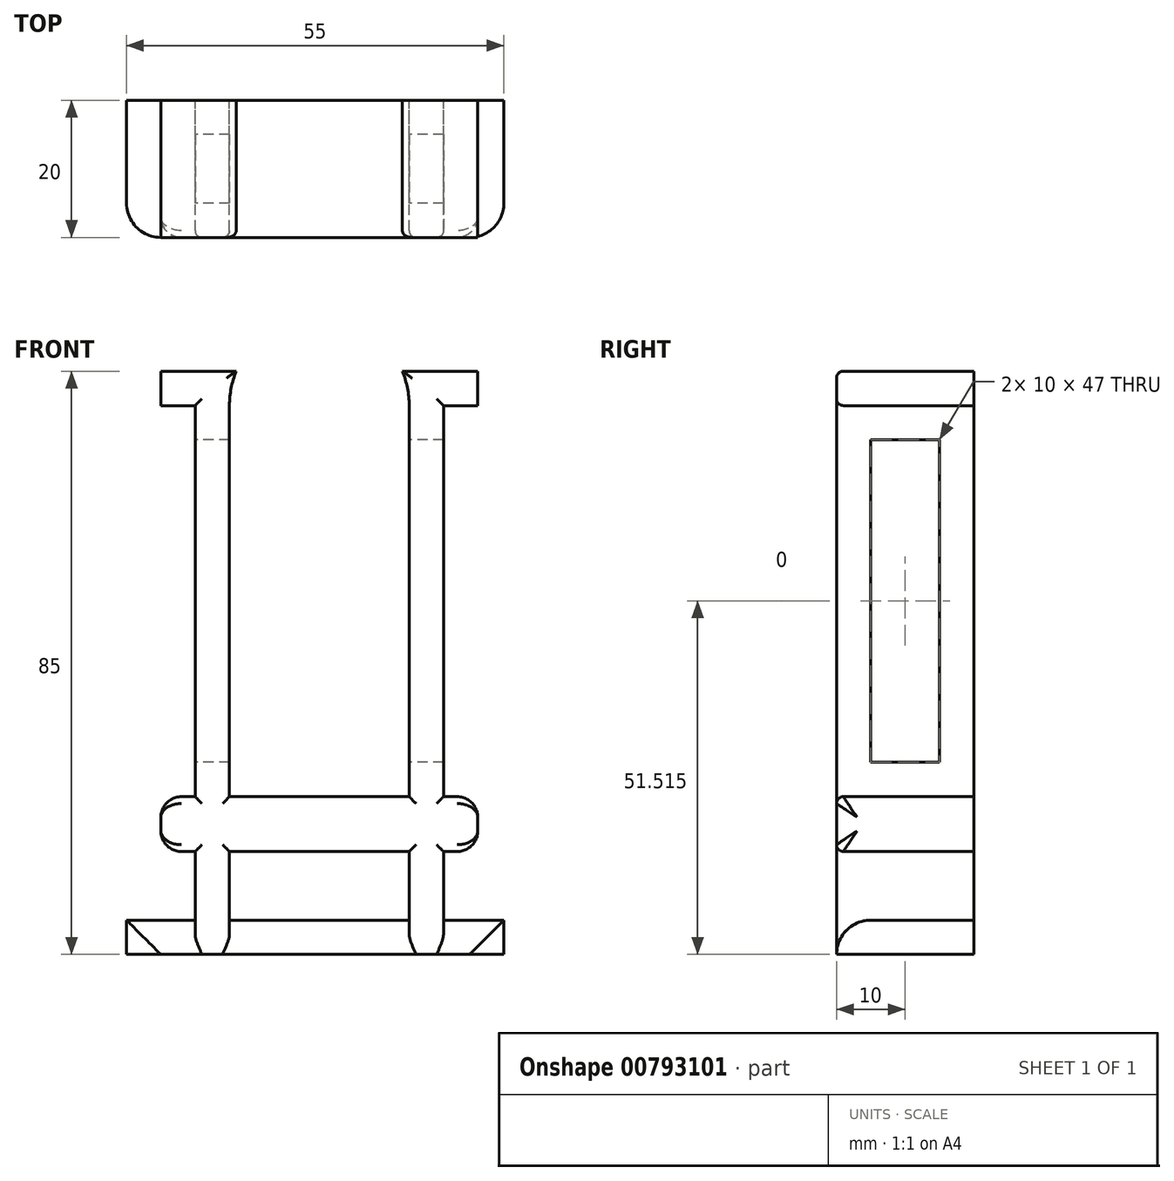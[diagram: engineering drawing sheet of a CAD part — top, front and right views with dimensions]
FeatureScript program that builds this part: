
annotation { "Feature Type Name" : "Feature", "Feature Type Description" : "" }
export const myFeature = defineFeature(function(context is Context, id is Id, definition is map)
    precondition{}
    {
        {
            var Q0;
            Q0=qCreatedBy(makeId("Front.planeOp"),FACE);
            var sketch = newSketch(context, id + "F0", { "sketchPlane" : qUnion([Q0])});
            skLineSegment(sketch, "E0.bottom", {"start": v(0, 0) * mm, "end": v(55, 0) * mm});
            skLineSegment(sketch, "E0.top", {"start": v(0, 5) * mm, "end": v(55, 5) * mm});
            skLineSegment(sketch, "E0.left", {"start": v(0, 0) * mm, "end": v(0, 5) * mm});
            skLineSegment(sketch, "E0.right", {"start": v(55, 0) * mm, "end": v(55, 5) * mm});
            skLineSegment(sketch, "E1.bottom", {"start": v(10, 5) * mm, "end": v(15, 5) * mm});
            skLineSegment(sketch, "E1.top", {"start": v(10, 15) * mm, "end": v(15, 15) * mm});
            skLineSegment(sketch, "E1.left", {"start": v(10, 5) * mm, "end": v(10, 15) * mm});
            skLineSegment(sketch, "E1.right", {"start": v(15, 5) * mm, "end": v(15, 15) * mm});
            skLineSegment(sketch, "E2.left", {"start": v(41.2, 5) * mm, "end": v(41.2, 15) * mm});
            skLineSegment(sketch, "E3.bottom", {"start": v(5, 23) * mm, "end": v(51.2, 23) * mm});
            skLineSegment(sketch, "E3.left", {"start": v(5, 23) * mm, "end": v(5, 15) * mm});
            skLineSegment(sketch, "E3.right", {"start": v(51.2, 23) * mm, "end": v(51.2, 15) * mm});
            skLineSegment(sketch, "E4.bottom", {"start": v(10, 23) * mm, "end": v(15, 23) * mm});
            skLineSegment(sketch, "E4.top", {"start": v(10, 80) * mm, "end": v(15, 80) * mm});
            skLineSegment(sketch, "E4.left", {"start": v(10, 23) * mm, "end": v(10, 80) * mm});
            skLineSegment(sketch, "E4.right", {"start": v(15, 23) * mm, "end": v(15, 80) * mm});
            skLineSegment(sketch, "E5.bottom", {"start": v(46.2, 23) * mm, "end": v(41.2, 23) * mm});
            skLineSegment(sketch, "E5.top", {"start": v(46.2, 80) * mm, "end": v(41.2, 80) * mm});
            skLineSegment(sketch, "E5.left", {"start": v(46.2, 23) * mm, "end": v(46.2, 80) * mm});
            skLineSegment(sketch, "E5.right", {"start": v(41.2, 23) * mm, "end": v(41.2, 80) * mm});
            skLineSegment(sketch, "E6.left", {"start": v(41.2, 15) * mm, "end": v(41.2, 15) * mm});
            skLineSegment(sketch, "E7", {"start": v(5, 15) * mm, "end": v(51.2, 15) * mm});
            skLineSegment(sketch, "E8.top", {"start": v(41.2, 5) * mm, "end": v(41.2, 5) * mm});
            skLineSegment(sketch, "E8.left", {"start": v(41.2, 15) * mm, "end": v(41.2, 5) * mm});
            skLineSegment(sketch, "E8.right", {"start": v(41.2, 15) * mm, "end": v(41.2, 5) * mm});
            skLineSegment(sketch, "E9.bottom", {"start": v(5, 80) * mm, "end": v(51.2, 80) * mm});
            skLineSegment(sketch, "E9.top", {"start": v(5, 85) * mm, "end": v(51.2, 85) * mm});
            skLineSegment(sketch, "E9.left", {"start": v(5, 80) * mm, "end": v(5, 85) * mm});
            skLineSegment(sketch, "E9.right", {"start": v(51.2, 80) * mm, "end": v(51.2, 85) * mm});
            skArc(sketch, "E10", {"start": v(10.8, 85) * mm, "mid": v(28.1, 98) * mm, "end": v(45.4, 85) * mm});
            skArc(sketch, "E11", {"start": v(15, 80) * mm, "mid": v(28.1, 93.1) * mm, "end": v(41.2, 80) * mm});
            skLineSegment(sketch, "E12", {"start": v(46.2, 15) * mm, "end": v(46.2, 5) * mm});
            skSolve(sketch);
        }
        {
            var Q0;
            {var subQ3=sQuery(id+"F0.wireOp",EDGE,"E10");Q0=makeQuery(id+"F0.imprint","IMPRINT",FACE,{"disambiguationData":[TD([[makeQuery(id+"F0.imprint","IMPRINT",EDGE,{"derivedFrom":subQ3}),-1.0]])]});}
            var Q1;
            {var subQ0=sQuery(id+"F0.wireOp",EDGE,"E11");var subQ4=sQuery(id+"F0.wireOp",EDGE,"E9.top");var subQ5=makeQuery(id+"F0.imprint","INTERSECT",VERTEX,{"disambiguationData":[OD(0.0)],"derivedFrom":[subQ4,subQ0]});Q1=makeQuery(id+"F0.imprint","IMPRINT",FACE,{"disambiguationData":[TD([[makeQuery(id+"F0.imprint","IMPRINT",EDGE,{"disambiguationData":[TD([[subQ5,-1.0]])],"derivedFrom":subQ4}),-1.0]])]});}
            var Q2;
            {var subQ6=sQuery(id+"F0.wireOp",EDGE,"E4.top");Q2=makeQuery(id+"F0.imprint","IMPRINT",FACE,{"disambiguationData":[TD([[makeQuery(id+"F0.imprint","IMPRINT",EDGE,{"derivedFrom":subQ6}),1.0]])]});}
            var Q3;
            {var subQ6=sQuery(id+"F0.wireOp",EDGE,"E5.top");Q3=makeQuery(id+"F0.imprint","IMPRINT",FACE,{"disambiguationData":[TD([[makeQuery(id+"F0.imprint","IMPRINT",EDGE,{"derivedFrom":subQ6}),-1.0]])]});}
            var Q4;
            Q4=makeQuery(id+"F0.imprint","IMPRINT",FACE,{"disambiguationData":[TD([[makeQuery(id+"F0.imprint","IMPRINT",EDGE,{"derivedFrom":sQuery(id+"F0.wireOp",EDGE,"E4.top")}),-1.0]])]});
            var Q5;
            Q5=makeQuery(id+"F0.imprint","IMPRINT",FACE,{"disambiguationData":[TD([[makeQuery(id+"F0.imprint","IMPRINT",EDGE,{"derivedFrom":sQuery(id+"F0.wireOp",EDGE,"E5.top")}),1.0]])]});
            var Q6;
            {var subQ7=sQuery(id+"F0.wireOp",EDGE,"E1.top");Q6=makeQuery(id+"F0.imprint","IMPRINT",FACE,{"disambiguationData":[TD([[makeQuery(id+"F0.imprint","IMPRINT",EDGE,{"derivedFrom":subQ7}),1.0]])]});}
            var Q7;
            Q7=makeQuery(id+"F0.imprint","IMPRINT",FACE,{"disambiguationData":[TD([[makeQuery(id+"F0.imprint","IMPRINT",EDGE,{"derivedFrom":sQuery(id+"F0.wireOp",EDGE,"E1.top")}),-1.0]])]});
            var Q8;
            {var subQ2=sQuery(id+"F0.wireOp",EDGE,"E2.left");Q8=makeQuery(id+"F0.imprint","IMPRINT",FACE,{"disambiguationData":[TD([[makeQuery(id+"F0.imprint","IMPRINT",EDGE,{"derivedFrom":subQ2}),-1.0]])]});}
            var Q9;
            Q9=makeQuery(id+"F0.imprint","IMPRINT",FACE,{"disambiguationData":[TD([[makeQuery(id+"F0.imprint","IMPRINT",EDGE,{"derivedFrom":sQuery(id+"F0.wireOp",EDGE,"E0.bottom")}),1.0]])]});
            extrude(context, id + "F1", {"entities" : qUnion([Q0, Q1, Q2, Q3, Q4, Q5, Q6, Q7, Q8, Q9]), "depth" : 20 * mm, "offsetDistance" : 25 * mm});
        }
        {
            var Q0;
            Q0=makeQuery(id+"F1.opExtrude","CAP_EDGE",EDGE,{"disambiguationData":[OSD([sQuery(id+"F0.wireOp",EDGE,"E4.left")])],"isStart":false});
            var Q1;
            Q1=makeQuery(id+"F1.opExtrude","CAP_EDGE",EDGE,{"disambiguationData":[OSD([sQuery(id+"F0.wireOp",EDGE,"E5.left")])],"isStart":false});
            var Q2;
            Q2=makeQuery(id+"F1.opExtrude","CAP_EDGE",EDGE,{"disambiguationData":[OSD([sQuery(id+"F0.wireOp",EDGE,"E5.right")])],"isStart":false});
            var Q3;
            Q3=makeQuery(id+"F1.opExtrude","CAP_EDGE",EDGE,{"disambiguationData":[OSD([sQuery(id+"F0.wireOp",EDGE,"E4.right")])],"isStart":false});
            var Q4;
            {var subQ0=sQuery(id+"F0.wireOp",EDGE,"E3.bottom");Q4=makeQuery(id+"F1.opExtrude","CAP_EDGE",EDGE,{"disambiguationData":[OSD([subQ0]),TDD([makeQuery(id+"F0.imprint","IMPRINT",EDGE,{"disambiguationData":[TD([[makeQuery(id+"F0.imprint","INTERSECT",VERTEX,{"derivedFrom":[subQ0,sQuery(id+"F0.wireOp",EDGE,"E4.right")]}),-1.0]])],"derivedFrom":subQ0})])],"isStart":false});}
            var Q5;
            {var subQ0=sQuery(id+"F0.wireOp",EDGE,"E7");Q5=makeQuery(id+"F1.opExtrude","CAP_EDGE",EDGE,{"disambiguationData":[OSD([subQ0]),TDD([makeQuery(id+"F0.imprint","IMPRINT",EDGE,{"disambiguationData":[TD([[makeQuery(id+"F0.imprint","INTERSECT",VERTEX,{"derivedFrom":[sQuery(id+"F0.wireOp",EDGE,"E2.left"),subQ0]}),1.0]])],"derivedFrom":subQ0})])],"isStart":false});}
            var Q6;
            Q6=makeQuery(id+"F1.opExtrude","CAP_EDGE",EDGE,{"disambiguationData":[OSD([sQuery(id+"F0.wireOp",EDGE,"E1.right")])],"isStart":false});
            var Q7;
            Q7=makeQuery(id+"F1.opExtrude","CAP_EDGE",EDGE,{"disambiguationData":[OSD([sQuery(id+"F0.wireOp",EDGE,"E2.left")])],"isStart":false});
            var Q8;
            Q8=makeQuery(id+"F1.opExtrude","CAP_EDGE",EDGE,{"disambiguationData":[OSD([sQuery(id+"F0.wireOp",EDGE,"E1.left")])],"isStart":false});
            var Q9;
            Q9=makeQuery(id+"F1.opExtrude","CAP_EDGE",EDGE,{"disambiguationData":[OSD([sQuery(id+"F0.wireOp",EDGE,"E12")])],"isStart":false});
            var Q10;
            {var subQ0=sQuery(id+"F0.wireOp",EDGE,"E11");var subQ1=sQuery(id+"F0.wireOp",EDGE,"E9.bottom");Q10=makeQuery(id+"F1.opExtrude","CAP_EDGE",EDGE,{"disambiguationData":[OSD([subQ1]),TDD([makeQuery(id+"F0.imprint","IMPRINT",EDGE,{"disambiguationData":[TD([[makeQuery(id+"F0.imprint","INTERSECT",VERTEX,{"derivedFrom":[sQuery(id+"F0.wireOp",EDGE,"E4.top"),sQuery(id+"F0.wireOp",EDGE,"E4.right"),subQ1,subQ0]}),-1.0]])],"derivedFrom":subQ1})])],"isStart":false});}
            var Q11;
            {var subQ0=sQuery(id+"F0.wireOp",EDGE,"E11");var subQ1=sQuery(id+"F0.wireOp",EDGE,"E9.top");Q11=makeQuery(id+"F1.opExtrude","CAP_EDGE",EDGE,{"disambiguationData":[OSD([subQ1]),TDD([makeQuery(id+"F0.imprint","IMPRINT",EDGE,{"disambiguationData":[TD([[makeQuery(id+"F0.imprint","INTERSECT",VERTEX,{"disambiguationData":[OD(0.0)],"derivedFrom":[subQ1,subQ0]}),-1.0]])],"derivedFrom":subQ1})])],"isStart":false});}
            var Q12;
            Q12=makeQuery(id+"F1.opExtrude","CAP_EDGE",EDGE,{"disambiguationData":[OSD([sQuery(id+"F0.wireOp",EDGE,"E11")])],"isStart":false});
            var Q13;
            Q13=makeQuery(id+"F1.opExtrude","CAP_EDGE",EDGE,{"disambiguationData":[OSD([sQuery(id+"F0.wireOp",EDGE,"E10")])],"isStart":false});
            var Q14;
            {var subQ0=sQuery(id+"F0.wireOp",EDGE,"E9.top");Q14=makeQuery(id+"F1.opExtrude","CAP_EDGE",EDGE,{"disambiguationData":[OSD([subQ0]),TDD([makeQuery(id+"F0.imprint","IMPRINT",EDGE,{"disambiguationData":[TD([[makeQuery(id+"F0.imprint","INTERSECT",VERTEX,{"derivedFrom":[subQ0,sQuery(id+"F0.wireOp",EDGE,"E9.left")]}),-1.0]])],"derivedFrom":subQ0})])],"isStart":false});}
            var Q15;
            {var subQ0=sQuery(id+"F0.wireOp",EDGE,"E9.top");Q15=makeQuery(id+"F1.opExtrude","CAP_EDGE",EDGE,{"disambiguationData":[OSD([subQ0]),TDD([makeQuery(id+"F0.imprint","IMPRINT",EDGE,{"disambiguationData":[TD([[makeQuery(id+"F0.imprint","INTERSECT",VERTEX,{"disambiguationData":[OD(0.0)],"derivedFrom":[subQ0,sQuery(id+"F0.wireOp",EDGE,"E10")]}),-1.0]])],"derivedFrom":subQ0})])],"isStart":false});}
            var Q16;
            {var subQ0=sQuery(id+"F0.wireOp",EDGE,"E9.bottom");Q16=makeQuery(id+"F1.opExtrude","CAP_EDGE",EDGE,{"disambiguationData":[OSD([subQ0]),TDD([makeQuery(id+"F0.imprint","IMPRINT",EDGE,{"disambiguationData":[TD([[makeQuery(id+"F0.imprint","INTERSECT",VERTEX,{"derivedFrom":[subQ0,sQuery(id+"F0.wireOp",EDGE,"E9.right")]}),1.0]])],"derivedFrom":subQ0})])],"isStart":false});}
            var Q17;
            {var subQ0=sQuery(id+"F0.wireOp",EDGE,"E9.bottom");Q17=makeQuery(id+"F1.opExtrude","CAP_EDGE",EDGE,{"disambiguationData":[OSD([subQ0]),TDD([makeQuery(id+"F0.imprint","IMPRINT",EDGE,{"disambiguationData":[TD([[makeQuery(id+"F0.imprint","INTERSECT",VERTEX,{"derivedFrom":[subQ0,sQuery(id+"F0.wireOp",EDGE,"E9.left")]}),-1.0]])],"derivedFrom":subQ0})])],"isStart":false});}
            var Q18;
            {var subQ0=sQuery(id+"F0.wireOp",EDGE,"E3.bottom");Q18=makeQuery(id+"F1.opExtrude","CAP_EDGE",EDGE,{"disambiguationData":[OSD([subQ0]),TDD([makeQuery(id+"F0.imprint","IMPRINT",EDGE,{"disambiguationData":[TD([[makeQuery(id+"F0.imprint","INTERSECT",VERTEX,{"derivedFrom":[subQ0,sQuery(id+"F0.wireOp",EDGE,"E3.left")]}),-1.0]])],"derivedFrom":subQ0})])],"isStart":false});}
            var Q19;
            {var subQ0=sQuery(id+"F0.wireOp",EDGE,"E7");Q19=makeQuery(id+"F1.opExtrude","CAP_EDGE",EDGE,{"disambiguationData":[OSD([subQ0]),TDD([makeQuery(id+"F0.imprint","IMPRINT",EDGE,{"disambiguationData":[TD([[makeQuery(id+"F0.imprint","INTERSECT",VERTEX,{"derivedFrom":[sQuery(id+"F0.wireOp",EDGE,"E3.left"),subQ0]}),-1.0]])],"derivedFrom":subQ0})])],"isStart":false});}
            var Q20;
            {var subQ0=sQuery(id+"F0.wireOp",EDGE,"E3.bottom");Q20=makeQuery(id+"F1.opExtrude","CAP_EDGE",EDGE,{"disambiguationData":[OSD([subQ0]),TDD([makeQuery(id+"F0.imprint","IMPRINT",EDGE,{"disambiguationData":[TD([[makeQuery(id+"F0.imprint","INTERSECT",VERTEX,{"derivedFrom":[subQ0,sQuery(id+"F0.wireOp",EDGE,"E3.right")]}),1.0]])],"derivedFrom":subQ0})])],"isStart":false});}
            var Q21;
            {var subQ0=sQuery(id+"F0.wireOp",EDGE,"E7");Q21=makeQuery(id+"F1.opExtrude","CAP_EDGE",EDGE,{"disambiguationData":[OSD([subQ0]),TDD([makeQuery(id+"F0.imprint","IMPRINT",EDGE,{"disambiguationData":[TD([[makeQuery(id+"F0.imprint","INTERSECT",VERTEX,{"derivedFrom":[sQuery(id+"F0.wireOp",EDGE,"E3.right"),subQ0]}),1.0]])],"derivedFrom":subQ0})])],"isStart":false});}
            fillet(context, id + "F2", {"entities" : qUnion([Q0, Q1, Q2, Q3, Q4, Q5, Q6, Q7, Q8, Q9, Q10, Q11, Q12, Q13, Q14, Q15, Q16, Q17, Q18, Q19, Q20, Q21]), "radius" : 1 * mm, "tangentPropagation" : true, "allowEdgeOverflow" : false});
        }
        {
            var Q0;
            Q0=makeQuery(id+"F1.opExtrude","SWEPT_EDGE",EDGE,{"disambiguationData":[OSD([sQuery(id+"F0.wireOp",EDGE,"E3.left"),sQuery(id+"F0.wireOp",EDGE,"E7")])]});
            var Q1;
            Q1=makeQuery(id+"F1.opExtrude","SWEPT_EDGE",EDGE,{"disambiguationData":[OSD([sQuery(id+"F0.wireOp",EDGE,"E3.right"),sQuery(id+"F0.wireOp",EDGE,"E7")])]});
            fillet(context, id + "F3", {"entities" : qUnion([Q0, Q1]), "radius" : 3 * mm, "tangentPropagation" : true, "allowEdgeOverflow" : false});
        }
        {
            var Q0;
            {var subQ0=sQuery(id+"F0.wireOp",EDGE,"E0.top");Q0=makeQuery(id+"F1.opExtrude","CAP_EDGE",EDGE,{"disambiguationData":[OSD([subQ0]),TDD([makeQuery(id+"F0.imprint","IMPRINT",EDGE,{"disambiguationData":[TD([[makeQuery(id+"F0.imprint","INTERSECT",VERTEX,{"derivedFrom":[subQ0,sQuery(id+"F0.wireOp",EDGE,"E0.left")]}),-1.0]])],"derivedFrom":subQ0})])],"isStart":false});}
            var Q1;
            {var subQ0=sQuery(id+"F0.wireOp",EDGE,"E0.top");Q1=makeQuery(id+"F1.opExtrude","CAP_EDGE",EDGE,{"disambiguationData":[OSD([subQ0]),TDD([makeQuery(id+"F0.imprint","IMPRINT",EDGE,{"disambiguationData":[TD([[makeQuery(id+"F0.imprint","INTERSECT",VERTEX,{"derivedFrom":[subQ0,sQuery(id+"F0.wireOp",EDGE,"E1.right")]}),-1.0]])],"derivedFrom":subQ0})])],"isStart":false});}
            var Q2;
            {var subQ0=sQuery(id+"F0.wireOp",EDGE,"E0.top");Q2=makeQuery(id+"F1.opExtrude","CAP_EDGE",EDGE,{"disambiguationData":[OSD([subQ0]),TDD([makeQuery(id+"F0.imprint","IMPRINT",EDGE,{"disambiguationData":[TD([[makeQuery(id+"F0.imprint","INTERSECT",VERTEX,{"derivedFrom":[subQ0,sQuery(id+"F0.wireOp",EDGE,"E12")]}),-1.0]])],"derivedFrom":subQ0})])],"isStart":false});}
            var Q3;
            Q3=makeQuery(id+"F1.opExtrude","CAP_EDGE",EDGE,{"disambiguationData":[OSD([sQuery(id+"F0.wireOp",EDGE,"E0.right")])],"isStart":false});
            var Q4;
            Q4=makeQuery(id+"F1.opExtrude","CAP_EDGE",EDGE,{"disambiguationData":[OSD([sQuery(id+"F0.wireOp",EDGE,"E0.left")])],"isStart":false});
            fillet(context, id + "F4", {"entities" : qUnion([Q0, Q1, Q2, Q3, Q4]), "radius" : 5 * mm, "tangentPropagation" : true, "allowEdgeOverflow" : false});
        }
        {
            var Q0;
            Q0=qCreatedBy(makeId("Right.planeOp"),FACE);
            var sketch = newSketch(context, id + "F5", { "sketchPlane" : qUnion([Q0])});
            skPoint(sketch, "E13", {"position": v(-5, 75.03) * mm});
            skPoint(sketch, "E14", {"position": v(-15, 75.02) * mm});
            skPoint(sketch, "E15", {"position": v(-18, 74.98) * mm});
            skSolve(sketch);
        }
        {
            var Q0;
            Q0=qCreatedBy(makeId("Right.planeOp"),FACE);
            var sketch = newSketch(context, id + "F6", { "sketchPlane" : qUnion([Q0])});
            skLineSegment(sketch, "E16.bottom", {"start": v(-5, 75.02) * mm, "end": v(-15, 75.02) * mm});
            skLineSegment(sketch, "E16.top", {"start": v(-5, 28.02) * mm, "end": v(-15, 28.02) * mm});
            skLineSegment(sketch, "E16.left", {"start": v(-5, 75.02) * mm, "end": v(-5, 28.02) * mm});
            skLineSegment(sketch, "E16.right", {"start": v(-15, 75.02) * mm, "end": v(-15, 28.02) * mm});
            skSolve(sketch);
        }
        {
            var Q0;
            Q0=makeQuery(id+"F6.imprint","IMPRINT",FACE,{"disambiguationData":[TD([[makeQuery(id+"F6.imprint","IMPRINT",EDGE,{"derivedFrom":sQuery(id+"F6.wireOp",EDGE,"E16.bottom")}),1.0]])]});
            extrude(context, id + "F7", {"entities" : qUnion([Q0]), "operationType" : NewBodyOperationType.REMOVE, "depth" : 60 * mm, "offsetDistance" : 25 * mm});
        }
    });
